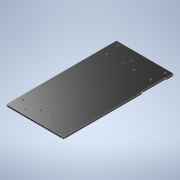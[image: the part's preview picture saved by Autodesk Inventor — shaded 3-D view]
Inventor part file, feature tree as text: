
AUTODESK INVENTOR PART (.ipt)
format: ipt  version: 2021 (Build 250183000, 183)  size: 178,176 bytes
history: native  units: mm
features: sketch x4, extrude x2, fillet x2, hole x2, projected_geometry x1
ambient origin geometry x8: Origin, YZ Plane, XZ Plane, XY Plane, X Axis, Y Axis, Z Axis, Center Point
bodies: Solid1 (feature_tree)
feature tree (11):
  extrude  "Extrusion1"  Depth=247.0mm
  extrude  "Extrusion2"  Depth=2.0mm
  fillet  "Fillet1"  Radius=4.0mm
  hole  "Hole1"  [1 undecoded]
  hole  "Hole2"  [1 undecoded]
  fillet  "Fillet2"  Radius=11.0mm
  sketch  "Sketch1"  dims[d0=128.5mm d1=247.0mm]
  sketch  "Sketch2"  dims[d2=4.0mm d3=0.0mm d6=2.0mm d7=4.0mm d8=0.0mm]
  sketch  "Sketch3"  dims[d9=18.0mm d10=70.0mm]
  sketch  "Sketch4"  dims[d11=1.0mm d12=11.0mm d13=11.0mm d14=11.0mm d15=27.25mm d16=13.5mm d17=13.5mm d18=32.0mm d19=32.0mm d20=3.8mm d21=6.0mm d22=4.0mm d23=2.0mm d24=90.0deg d25=8.0mm d26=20.594885mm d27=8.0mm d28=8.0mm d29=8.5mm d30=22.0mm d31=37.0mm d32=15.0mm d33=15.0mm d34=12.5mm d35=12.5mm d36=3.8mm d37=6.0mm d38=4.0mm d39=2.0mm d40=90.0deg d41=8.0mm d42=20.594885mm d43=2.0mm]
  projected_geometry  "Projected Loop1"
note: 2 required parameter values undecoded (feature->parameter linkage not recoverable at this tier; creation-order binding heuristic only, values carry confidence <= 0.55)
